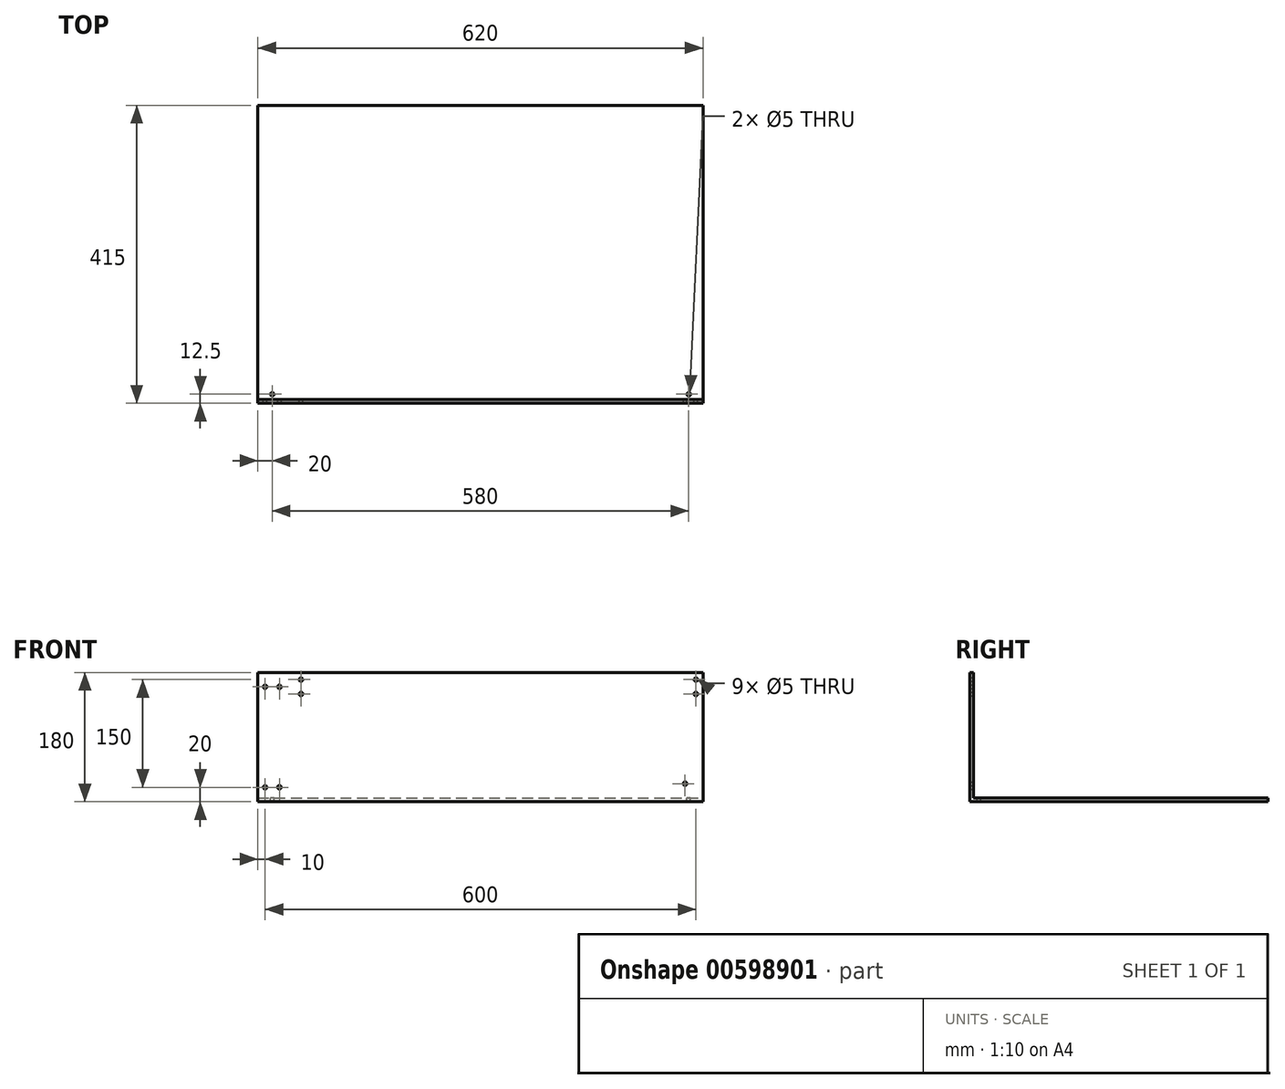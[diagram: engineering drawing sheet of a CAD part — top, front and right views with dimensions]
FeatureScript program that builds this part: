
annotation { "Feature Type Name" : "Feature", "Feature Type Description" : "" }
export const myFeature = defineFeature(function(context is Context, id is Id, definition is map)
    precondition{}
    {
        {
            var Q0;
            Q0=qCreatedBy(makeId("Top.planeOp"),FACE);
            var sketch = newSketch(context, id + "F0", { "sketchPlane" : qUnion([Q0])});
            skLineSegment(sketch, "E0.bottom", {"start": v(310, -207.5) * mm, "end": v(-310, -207.5) * mm});
            skLineSegment(sketch, "E0.top", {"start": v(310, 207.5) * mm, "end": v(-310, 207.5) * mm});
            skLineSegment(sketch, "E0.left", {"start": v(310, -207.5) * mm, "end": v(310, 207.5) * mm});
            skLineSegment(sketch, "E0.right", {"start": v(-310, -207.5) * mm, "end": v(-310, 207.5) * mm});
            skPoint(sketch, "E0.middle", {"position": v(0, 0) * mm});
            skSolve(sketch);
        }
        {
            var Q0;
            Q0=qSketchRegion(id+"F0",true);
            extrude(context, id + "F1", {"entities" : qUnion([Q0]), "depth" : 5 * mm, "offsetDistance" : 25 * mm});
        }
        {
            var Q0;
            Q0=makeQuery(id+"F1.opExtrude","CAP_FACE",FACE,{"disambiguationData":[OSD([sQuery(id+"F0.wireOp",EDGE,"E0.bottom"),sQuery(id+"F0.wireOp",EDGE,"E0.top"),sQuery(id+"F0.wireOp",EDGE,"E0.left"),sQuery(id+"F0.wireOp",EDGE,"E0.right")])],"isStart":false});
            var sketch = newSketch(context, id + "F2", { "sketchPlane" : qUnion([Q0])});
            skLineSegment(sketch, "E1", {"start": v(-310, -202.5) * mm, "end": v(310, -202.5) * mm});
            skLineSegment(sketch, "E2", {"start": v(310, -202.5) * mm, "end": v(310, -207.5) * mm});
            skLineSegment(sketch, "E3", {"start": v(310, -207.5) * mm, "end": v(-310, -207.5) * mm});
            skLineSegment(sketch, "E4", {"start": v(-310, -207.5) * mm, "end": v(-310, -202.5) * mm});
            skSolve(sketch);
        }
        {
            var Q0;
            Q0=makeQuery(id+"F2.imprint","IMPRINT",FACE,{"disambiguationData":[TD([[makeQuery(id+"F2.imprint","IMPRINT",EDGE,{"derivedFrom":sQuery(id+"F2.wireOp",EDGE,"E1")}),-1.0]])]});
            extrude(context, id + "F3", {"entities" : qUnion([Q0]), "operationType" : NewBodyOperationType.ADD, "depth" : 175 * mm, "offsetDistance" : 25 * mm});
        }
        {
            var Q0;
            Q0=makeQuery(id+"F3.boolean.opBoolean","MERGE",FACE,{"derivedFrom":[makeQuery(id+"F1.opExtrude","SWEPT_FACE",FACE,{"disambiguationData":[OSD([sQuery(id+"F0.wireOp",EDGE,"E0.bottom")])]}),makeQuery(id+"F3.opExtrude","SWEPT_FACE",FACE,{"disambiguationData":[OSD([sQuery(id+"F2.wireOp",EDGE,"E3")])]})]});
            var sketch = newSketch(context, id + "F4", { "sketchPlane" : qUnion([Q0])});
            skLineSegment(sketch, "E5", {"start": v(300, 180) * mm, "end": v(300, 138.82) * mm, "construction": true});
            skPoint(sketch, "E6", {"position": v(300, 170) * mm});
            skPoint(sketch, "E7", {"position": v(300, 150) * mm});
            skSolve(sketch);
        }
        {
            var Q0;
            Q0=sQuery(id+"F4.wireOp",VERTEX,"E6");
            var Q1;
            Q1=makeQuery(id+"F1.opExtrude","SWEPT_BODY",BODY,{"disambiguationData":[OSD([sQuery(id+"F0.wireOp",EDGE,"E0.bottom"),sQuery(id+"F0.wireOp",EDGE,"E0.top"),sQuery(id+"F0.wireOp",EDGE,"E0.left"),sQuery(id+"F0.wireOp",EDGE,"E0.right")])]});
            hole(context, id + "F5", {"style" : HoleStyle.SIMPLE, "endStyle" : HoleEndStyle.THROUGH, "holeDiameter" : 5 * mm, "majorDiameter" : 5 * mm, "isTappedThrough" : true, "tappedDepth" : 12 * mm, "tapClearance" : 3, "locations" : qUnion([Q0]), "scope" : qUnion([Q1])});
        }
        {
            var Q0;
            Q0=makeQuery(id+"F3.boolean.opBoolean","MERGE",FACE,{"derivedFrom":[makeQuery(id+"F1.opExtrude","SWEPT_FACE",FACE,{"disambiguationData":[OSD([sQuery(id+"F0.wireOp",EDGE,"E0.bottom")])]}),makeQuery(id+"F3.opExtrude","SWEPT_FACE",FACE,{"disambiguationData":[OSD([sQuery(id+"F2.wireOp",EDGE,"E3")])]})]});
            var sketch = newSketch(context, id + "F6", { "sketchPlane" : qUnion([Q0])});
            skLineSegment(sketch, "E8", {"start": v(300, 180) * mm, "end": v(300, 144.67) * mm, "construction": true});
            skPoint(sketch, "E9", {"position": v(300, 150) * mm});
            skSolve(sketch);
        }
        {
            var Q0;
            Q0=sQuery(id+"F6.wireOp",VERTEX,"E9");
            var Q1;
            Q1=makeQuery(id+"F1.opExtrude","SWEPT_BODY",BODY,{"disambiguationData":[OSD([sQuery(id+"F0.wireOp",EDGE,"E0.bottom"),sQuery(id+"F0.wireOp",EDGE,"E0.top"),sQuery(id+"F0.wireOp",EDGE,"E0.left"),sQuery(id+"F0.wireOp",EDGE,"E0.right")])]});
            hole(context, id + "F7", {"style" : HoleStyle.SIMPLE, "endStyle" : HoleEndStyle.THROUGH, "holeDiameter" : 5 * mm, "majorDiameter" : 5 * mm, "isTappedThrough" : true, "tappedDepth" : 12 * mm, "tapClearance" : 3, "locations" : qUnion([Q0]), "scope" : qUnion([Q1])});
        }
        {
            var Q0;
            Q0=makeQuery(id+"F3.boolean.opBoolean","MERGE",FACE,{"derivedFrom":[makeQuery(id+"F1.opExtrude","SWEPT_FACE",FACE,{"disambiguationData":[OSD([sQuery(id+"F0.wireOp",EDGE,"E0.bottom")])]}),makeQuery(id+"F3.opExtrude","SWEPT_FACE",FACE,{"disambiguationData":[OSD([sQuery(id+"F2.wireOp",EDGE,"E3")])]})]});
            var sketch = newSketch(context, id + "F8", { "sketchPlane" : qUnion([Q0])});
            skLineSegment(sketch, "E10", {"start": v(-250, 180) * mm, "end": v(-250, 162.68) * mm, "construction": true});
            skPoint(sketch, "E11", {"position": v(-250, 170) * mm});
            skSolve(sketch);
        }
        {
            var Q0;
            Q0=sQuery(id+"F8.wireOp",VERTEX,"E11");
            var Q1;
            Q1=makeQuery(id+"F1.opExtrude","SWEPT_BODY",BODY,{"disambiguationData":[OSD([sQuery(id+"F0.wireOp",EDGE,"E0.bottom"),sQuery(id+"F0.wireOp",EDGE,"E0.top"),sQuery(id+"F0.wireOp",EDGE,"E0.left"),sQuery(id+"F0.wireOp",EDGE,"E0.right")])]});
            hole(context, id + "F9", {"style" : HoleStyle.SIMPLE, "endStyle" : HoleEndStyle.THROUGH, "holeDiameter" : 5 * mm, "majorDiameter" : 5 * mm, "isTappedThrough" : true, "tappedDepth" : 12 * mm, "tapClearance" : 3, "locations" : qUnion([Q0]), "scope" : qUnion([Q1])});
        }
        {
            var Q0;
            Q0=makeQuery(id+"F3.boolean.opBoolean","MERGE",FACE,{"derivedFrom":[makeQuery(id+"F1.opExtrude","SWEPT_FACE",FACE,{"disambiguationData":[OSD([sQuery(id+"F0.wireOp",EDGE,"E0.bottom")])]}),makeQuery(id+"F3.opExtrude","SWEPT_FACE",FACE,{"disambiguationData":[OSD([sQuery(id+"F2.wireOp",EDGE,"E3")])]})]});
            var sketch = newSketch(context, id + "F10", { "sketchPlane" : qUnion([Q0])});
            skLineSegment(sketch, "E12", {"start": v(-250, 180) * mm, "end": v(-250, 135.53) * mm, "construction": true});
            skPoint(sketch, "E13", {"position": v(-250, 150) * mm});
            skSolve(sketch);
        }
        {
            var Q0;
            Q0=sQuery(id+"F10.wireOp",VERTEX,"E13");
            var Q1;
            Q1=makeQuery(id+"F1.opExtrude","SWEPT_BODY",BODY,{"disambiguationData":[OSD([sQuery(id+"F0.wireOp",EDGE,"E0.bottom"),sQuery(id+"F0.wireOp",EDGE,"E0.top"),sQuery(id+"F0.wireOp",EDGE,"E0.left"),sQuery(id+"F0.wireOp",EDGE,"E0.right")])]});
            hole(context, id + "F11", {"style" : HoleStyle.SIMPLE, "endStyle" : HoleEndStyle.THROUGH, "holeDiameter" : 5 * mm, "majorDiameter" : 5 * mm, "isTappedThrough" : true, "tappedDepth" : 12 * mm, "tapClearance" : 3, "locations" : qUnion([Q0]), "scope" : qUnion([Q1])});
        }
        {
            var Q0;
            Q0=makeQuery(id+"F3.boolean.opBoolean","MERGE",FACE,{"derivedFrom":[makeQuery(id+"F1.opExtrude","SWEPT_FACE",FACE,{"disambiguationData":[OSD([sQuery(id+"F0.wireOp",EDGE,"E0.bottom")])]}),makeQuery(id+"F3.opExtrude","SWEPT_FACE",FACE,{"disambiguationData":[OSD([sQuery(id+"F2.wireOp",EDGE,"E3")])]})]});
            var sketch = newSketch(context, id + "F12", { "sketchPlane" : qUnion([Q0])});
            skLineSegment(sketch, "E14", {"start": v(-310, 160) * mm, "end": v(-280, 160) * mm, "construction": true});
            skPoint(sketch, "E15", {"position": v(-300, 160) * mm});
            skSolve(sketch);
        }
        {
            var Q0;
            Q0=makeQuery(id+"F3.boolean.opBoolean","MERGE",FACE,{"derivedFrom":[makeQuery(id+"F1.opExtrude","SWEPT_FACE",FACE,{"disambiguationData":[OSD([sQuery(id+"F0.wireOp",EDGE,"E0.bottom")])]}),makeQuery(id+"F3.opExtrude","SWEPT_FACE",FACE,{"disambiguationData":[OSD([sQuery(id+"F2.wireOp",EDGE,"E3")])]})]});
            var sketch = newSketch(context, id + "F13", { "sketchPlane" : qUnion([Q0])});
            skLineSegment(sketch, "E16", {"start": v(-310, 20) * mm, "end": v(-280, 20) * mm, "construction": true});
            skPoint(sketch, "E17", {"position": v(-300, 20) * mm});
            skSolve(sketch);
        }
        {
            var Q0;
            Q0=makeQuery(id+"F1.opExtrude","CAP_FACE",FACE,{"disambiguationData":[OSD([sQuery(id+"F0.wireOp",EDGE,"E0.bottom"),sQuery(id+"F0.wireOp",EDGE,"E0.top"),sQuery(id+"F0.wireOp",EDGE,"E0.left"),sQuery(id+"F0.wireOp",EDGE,"E0.right")])],"isStart":true});
            var sketch = newSketch(context, id + "F14", { "sketchPlane" : qUnion([Q0])});
            skLineSegment(sketch, "E18", {"start": v(290, 207.5) * mm, "end": v(290, 195) * mm});
            skSolve(sketch);
        }
        {
            var Q0;
            Q0=sQuery(id+"F14.wireOp",VERTEX,"E18.end");
            var Q1;
            Q1=makeQuery(id+"F1.opExtrude","SWEPT_BODY",BODY,{"disambiguationData":[OSD([sQuery(id+"F0.wireOp",EDGE,"E0.bottom"),sQuery(id+"F0.wireOp",EDGE,"E0.top"),sQuery(id+"F0.wireOp",EDGE,"E0.left"),sQuery(id+"F0.wireOp",EDGE,"E0.right")])]});
            hole(context, id + "F15", {"style" : HoleStyle.SIMPLE, "endStyle" : HoleEndStyle.THROUGH, "holeDiameter" : 5 * mm, "majorDiameter" : 5 * mm, "isTappedThrough" : true, "tappedDepth" : 12 * mm, "tapClearance" : 3, "locations" : qUnion([Q0]), "scope" : qUnion([Q1])});
        }
        {
            var Q0;
            Q0=makeQuery(id+"F1.opExtrude","CAP_FACE",FACE,{"disambiguationData":[OSD([sQuery(id+"F0.wireOp",EDGE,"E0.bottom"),sQuery(id+"F0.wireOp",EDGE,"E0.top"),sQuery(id+"F0.wireOp",EDGE,"E0.left"),sQuery(id+"F0.wireOp",EDGE,"E0.right")])],"isStart":true});
            var sketch = newSketch(context, id + "F16", { "sketchPlane" : qUnion([Q0])});
            skLineSegment(sketch, "E19", {"start": v(-290, 207.5) * mm, "end": v(-290, 195) * mm});
            skSolve(sketch);
        }
        {
            var Q0;
            Q0=sQuery(id+"F16.wireOp",VERTEX,"E19.end");
            var Q1;
            Q1=makeQuery(id+"F1.opExtrude","SWEPT_BODY",BODY,{"disambiguationData":[OSD([sQuery(id+"F0.wireOp",EDGE,"E0.bottom"),sQuery(id+"F0.wireOp",EDGE,"E0.top"),sQuery(id+"F0.wireOp",EDGE,"E0.left"),sQuery(id+"F0.wireOp",EDGE,"E0.right")])]});
            hole(context, id + "F17", {"style" : HoleStyle.SIMPLE, "endStyle" : HoleEndStyle.THROUGH, "holeDiameter" : 5 * mm, "majorDiameter" : 5 * mm, "isTappedThrough" : true, "tappedDepth" : 12 * mm, "tapClearance" : 3, "locations" : qUnion([Q0]), "scope" : qUnion([Q1])});
        }
        {
            var Q0;
            Q0=makeQuery(id+"F3.boolean.opBoolean","MERGE",FACE,{"derivedFrom":[makeQuery(id+"F1.opExtrude","SWEPT_FACE",FACE,{"disambiguationData":[OSD([sQuery(id+"F0.wireOp",EDGE,"E0.bottom")])]}),makeQuery(id+"F3.opExtrude","SWEPT_FACE",FACE,{"disambiguationData":[OSD([sQuery(id+"F2.wireOp",EDGE,"E3")])]})]});
            var sketch = newSketch(context, id + "F18", { "sketchPlane" : qUnion([Q0])});
            skLineSegment(sketch, "E20", {"start": v(285, 0) * mm, "end": v(285, 25) * mm});
            skSolve(sketch);
        }
        {
            var Q0;
            Q0=sQuery(id+"F18.wireOp",VERTEX,"E20.end");
            var Q1;
            Q1=makeQuery(id+"F1.opExtrude","SWEPT_BODY",BODY,{"disambiguationData":[OSD([sQuery(id+"F0.wireOp",EDGE,"E0.bottom"),sQuery(id+"F0.wireOp",EDGE,"E0.top"),sQuery(id+"F0.wireOp",EDGE,"E0.left"),sQuery(id+"F0.wireOp",EDGE,"E0.right")])]});
            hole(context, id + "F19", {"style" : HoleStyle.SIMPLE, "endStyle" : HoleEndStyle.BLIND, "holeDiameter" : 5 * mm, "majorDiameter" : 5 * mm, "holeDepth" : 11 * mm, "isTappedThrough" : true, "tappedDepth" : 12 * mm, "tapClearance" : 3, "locations" : qUnion([Q0]), "scope" : qUnion([Q1])});
        }
        {
            var Q0;
            Q0=sQuery(id+"F13.wireOp",VERTEX,"E17");
            var Q1;
            Q1=sQuery(id+"F13.wireOp",VERTEX,"E16.end");
            var Q2;
            Q2=sQuery(id+"F12.wireOp",VERTEX,"E15");
            var Q3;
            Q3=sQuery(id+"F12.wireOp",VERTEX,"E14.end");
            var Q4;
            Q4=makeQuery(id+"F1.opExtrude","SWEPT_BODY",BODY,{"disambiguationData":[OSD([sQuery(id+"F0.wireOp",EDGE,"E0.bottom"),sQuery(id+"F0.wireOp",EDGE,"E0.top"),sQuery(id+"F0.wireOp",EDGE,"E0.left"),sQuery(id+"F0.wireOp",EDGE,"E0.right")])]});
            hole(context, id + "F20", {"style" : HoleStyle.SIMPLE, "endStyle" : HoleEndStyle.BLIND, "holeDiameter" : 5 * mm, "majorDiameter" : 5 * mm, "holeDepth" : 11 * mm, "isTappedThrough" : true, "tappedDepth" : 12 * mm, "tapClearance" : 3, "startFromSketch" : true, "locations" : qUnion([Q0, Q1, Q2, Q3]), "scope" : qUnion([Q4])});
        }
    });
